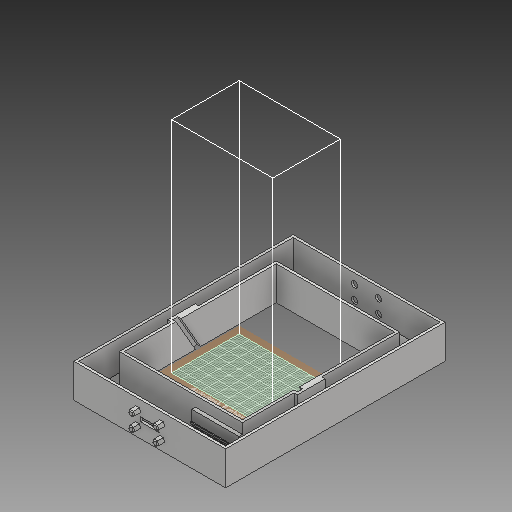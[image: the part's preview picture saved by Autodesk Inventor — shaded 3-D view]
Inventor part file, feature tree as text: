
AUTODESK INVENTOR PART (.ipt)
format: ipt  version: 2018.3 (Build 223284000, 284)  size: 665,600 bytes
history: native  units: mm
features: extrude x14, sketch x14, chamfer x3
ambient origin geometry x8: Origin, YZ Plane, XZ Plane, XY Plane, X Axis, Y Axis, Z Axis, Center Point
bodies: Solid1 (feature_tree)
feature tree (31):
  extrude  "Extrusion1"  Depth=130.0mm
  extrude  "Extrusion2"  Depth=90.0mm
  extrude  "Extrusion3"  TaperAngle=210.0deg  [1 undecoded]
  extrude  "Extrusion4"  Depth=2.0mm
  chamfer  "Chamfer1"  Distance=2.0mm
  extrude  "Extrusion5"  Depth=3.0mm
  chamfer  "Chamfer2"  Distance=2.0mm
  extrude  "Extrusion6"  Depth=20.0mm
  extrude  "Extrusion7"  Depth=20.0mm
  extrude  "Extrusion8"  Depth=3.0mm
  extrude  "Extrusion9"  Depth=35.0mm
  extrude  "Extrusion10"  Depth=35.0mm
  extrude  "Extrusion11"  Depth=1.1mm
  extrude  "Extrusion12"  Depth=12.11mm
  extrude  "Extrusion13"  Depth=2.0mm
  extrude  "Extrusion14"  Depth=2.0mm
  chamfer  "Chamfer3"  Distance=4.83mm
  sketch  "Sketch1"  dims[d0=90.0mm d1=130.0mm]
  sketch  "Sketch2"  dims[d2=70.0mm d3=90.0mm]
  sketch  "Sketch3"  dims[d4=20.0mm d5=0.0mm d6=210.0deg]
  sketch  "Sketch4"  dims[d7=3.0mm d8=26.471143mm d9=2.0mm d10=0.0mm]
  sketch  "Sketch5"  dims[d11=30.0deg d12=3.0mm]
  sketch  "Sketch6"  dims[d13=26.471143mm d14=2.0mm d15=0.0mm]
  sketch  "Sketch7"  dims[d16=20.0mm d17=20.0mm]
  sketch  "Sketch8"  dims[d18=10.0mm d19=20.0mm]
  sketch  "Sketch9"  dims[d20=14.0mm d21=3.0mm]
  sketch  "Sketch10"  dims[d22=3.0mm d23=35.0mm]
  sketch  "Sketch11"  dims[d24=35.0mm d25=1.45mm]
  sketch  "Sketch12"  dims[d26=1.45mm d27=1.1mm]
  sketch  "Sketch13"  dims[d28=1.1mm d29=12.11mm]
  sketch  "Sketch14"  dims[d30=1.13mm d31=1.13mm d32=4.83mm d33=4.83mm d34=1.129mm d35=1.128692mm d36=4.0mm d37=0.0mm d38=0.5mm d39=2.0mm d40=45.0deg d41=20.0mm d42=14.0mm d43=3.0mm d44=3.0mm d45=35.0mm d46=35.0mm d74=4.0mm d75=0.0mm d76=0.5mm d77=2.0mm d78=45.0deg d79=128.5mm d80=87.0mm d81=127.0mm d82=46.0mm d83=2.0mm d84=16.434mm d85=2.0mm d86=30.566mm d87=73.0mm d88=2.0mm d89=18.0mm d90=0.0mm d100=11.0mm d101=2.6mm d102=8.7mm d103=39.5mm d104=39.5mm d105=8.7mm d106=10.0mm d107=0.0mm d108=28.0mm d109=6.0mm d110=2.2mm d111=0.0mm d114=28.0mm d115=12.0mm d116=7.0mm d117=2.2mm d118=0.0mm d119=1.0mm d120=0.0mm d121=8.8mm d122=1.0mm d123=6.0mm d124=0.55mm d125=0.0mm d126=0.6mm d127=0.0mm d128=1.0mm d129=1.0mm d130=6.2mm d131=1.8mm d132=0.55mm d133=0.0mm d134=0.6mm d135=0.0mm d136=7.0mm d137=0.0mm d138=6.0mm d139=2.0mm d140=1.745329mm d141=1.45mm d142=2.15mm d143=1.13mm d144=2.15mm d145=1.13mm d146=1.1mm d148=2.15mm d149=1.1mm d150=1.128mm d151=4.83298mm d153=12.113227mm d154=2.15mm d155=1.128mm d156=1.45mm d157=4.83298mm d158=12.113227mm]
note: 1 required parameter value undecoded (feature->parameter linkage not recoverable at this tier; creation-order binding heuristic only, values carry confidence <= 0.55)
